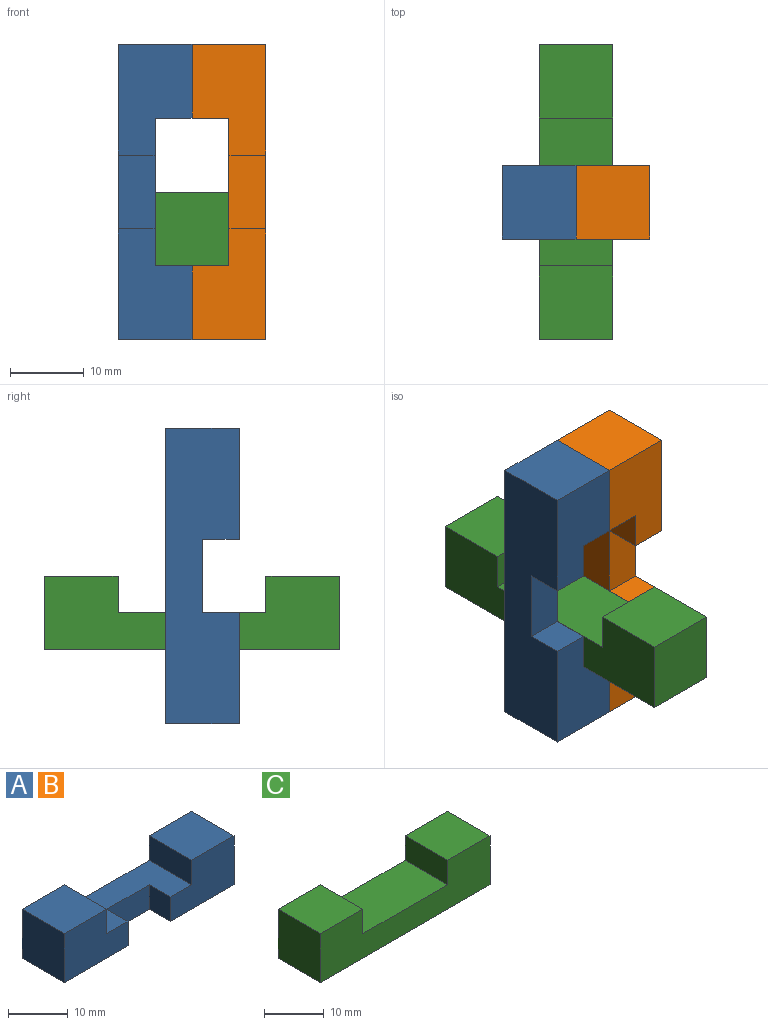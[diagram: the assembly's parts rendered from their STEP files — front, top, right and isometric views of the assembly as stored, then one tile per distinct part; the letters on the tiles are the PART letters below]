
ASSEMBLY  parts=3 mates=2
PART A: 14 faces, bbox 40x10x10 mm
  f0: plane 15x10mm, normal (0,-1,0), area 125mm2, adj f1,f3,f6,f9,f10,f11
  f1: plane 40x10mm, normal (0,0,-1), area 350mm2, adj f0,f2,f4,f5,f6,f11,f12,f13
  f2: plane 15x10mm, normal (0,-1,0), area 125mm2, adj f1,f5,f7,f8,f9,f12
  f3: plane 10x10mm, normal (0,0,1), area 100mm2, adj f0,f4,f6,f10
  f4: plane 40x10mm, normal (0,1,0), area 300mm2, adj f1,f3,f5,f6,f7,f8,f9,f10
  f5: plane 10x10mm, normal (-1,0,0), area 100mm2, adj f1,f2,f4,f7
  f6: plane 10x10mm, normal (1,0,0), area 100mm2, adj f0,f1,f3,f4
  f7: plane 10x10mm, normal (0,0,1), area 100mm2, adj f2,f4,f5,f8
  f8: plane 10x5mm, normal (1,0,0), area 50mm2, adj f2,f4,f7,f9
  f9: plane 20x10mm, normal (0,0,1), area 150mm2, adj f0,f2,f4,f8,f10,f11,f12,f13
  f10: plane 10x5mm, normal (-1,0,0), area 50mm2, adj f0,f3,f4,f9
  f11: plane 5x5mm, normal (-1,0,0), area 25mm2, adj f0,f1,f9,f13
  f12: plane 5x5mm, normal (1,0,0), area 25mm2, adj f1,f2,f9,f13
  f13: plane 10x5mm, normal (0,-1,0), area 50mm2, adj f1,f9,f11,f12
PART B: same geometry as A
PART C: 10 faces, bbox 40x10x10 mm
  f0: plane 40x10mm, normal (0,-1,0), area 300mm2, adj f1,f3,f4,f5,f6,f7,f8,f9
  f1: plane 10x10mm, normal (0,0,1), area 100mm2, adj f0,f2,f4,f9
  f2: plane 40x10mm, normal (0,1,0), area 300mm2, adj f1,f3,f4,f5,f6,f7,f8,f9
  f3: plane 10x10mm, normal (-1,0,0), area 100mm2, adj f0,f2,f5,f6
  f4: plane 10x10mm, normal (1,0,0), area 100mm2, adj f0,f1,f2,f6
  f5: plane 10x10mm, normal (0,0,1), area 100mm2, adj f0,f2,f3,f7
  f6: plane 40x10mm, normal (0,0,-1), area 400mm2, adj f0,f2,f3,f4
  f7: plane 10x5mm, normal (1,0,0), area 50mm2, adj f0,f2,f5,f8
  f8: plane 20x10mm, normal (0,0,1), area 200mm2, adj f0,f2,f7,f9
  f9: plane 10x5mm, normal (-1,0,0), area 50mm2, adj f0,f1,f2,f8
PLACE A rot(axis=(0,1,0),90deg) t=(-10,5,20)mm
PLACE B rot(axis=(0,-1,0),90deg) t=(10,5,20)mm
PLACE C rot(axis=(0,0,1),90deg) t=(0,6.4,10)mm
MATE fastened B.f3 <-> A.f7  axis (-1,0,0) through (0,5,35)mm
MATE slider A.f0 <-> C.f4  axis (0,-1,0) through (0,0,10)mm
